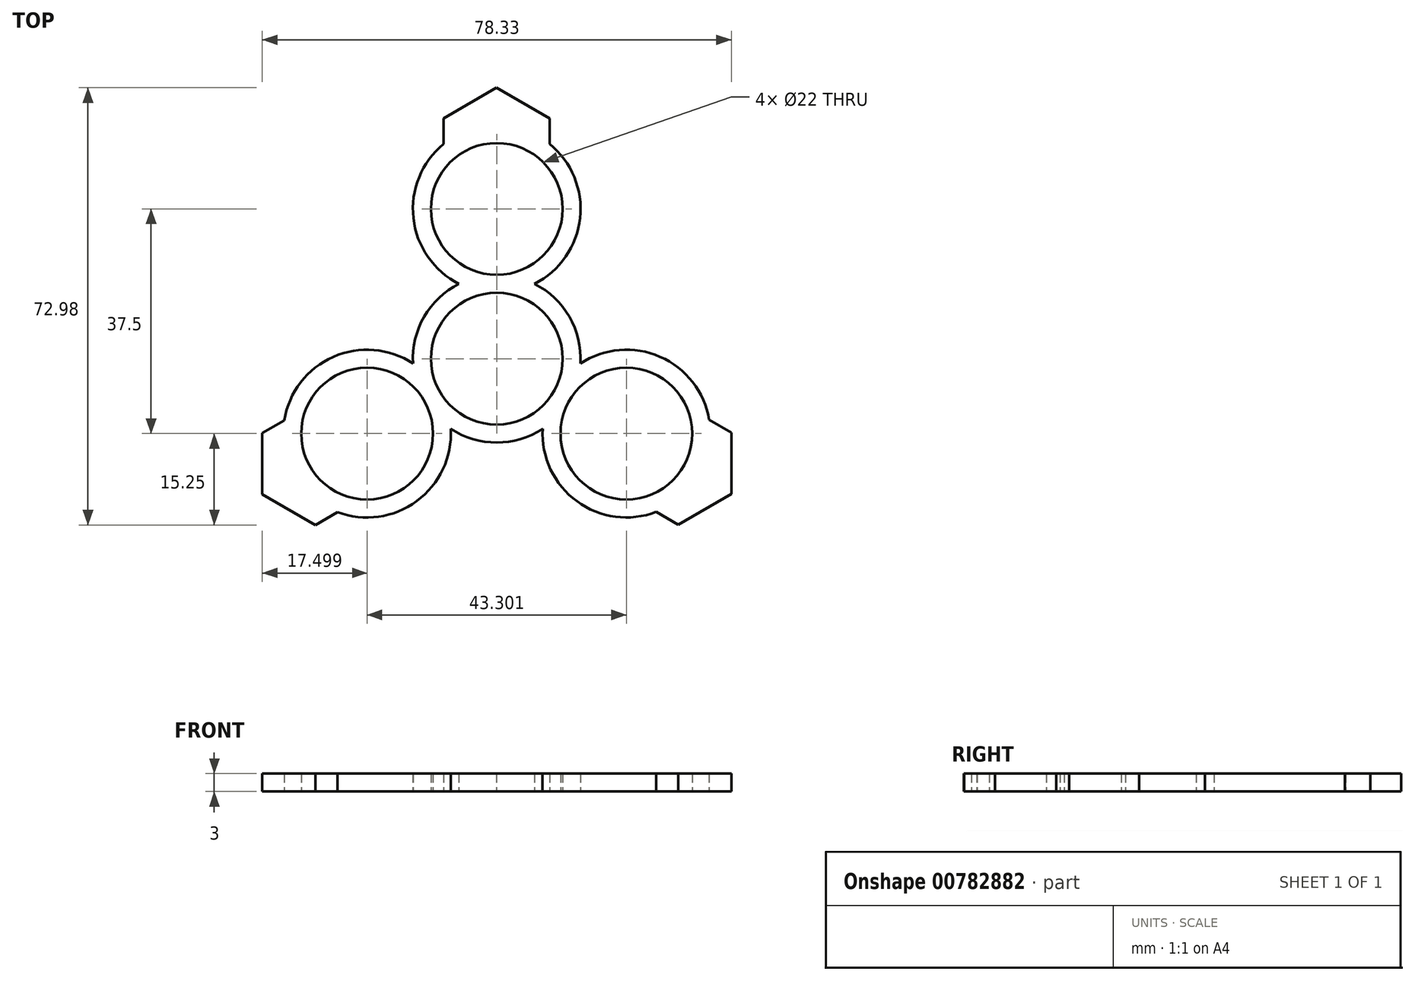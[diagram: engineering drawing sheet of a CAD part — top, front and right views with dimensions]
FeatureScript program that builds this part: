
annotation { "Feature Type Name" : "Feature", "Feature Type Description" : "" }
export const myFeature = defineFeature(function(context is Context, id is Id, definition is map)
    precondition{}
    {
        {
            var Q0;
            Q0=qCreatedBy(makeId("Top.planeOp"),FACE);
            var sketch = newSketch(context, id + "F0", { "sketchPlane" : qUnion([Q0])});
            skArc(sketch, "E0.1.0", {"start": v(-7.67, -11.71) * mm, "mid": v(-4, -13.42) * mm, "end": v(0, -14) * mm});
            skCircle(sketch, "E0.1.1", {"center": v(-21.65, -12.5) * mm, "radius": 11 * mm});
            skArc(sketch, "E0.1.2", {"start": v(-12.12, 7) * mm, "mid": v(-13.62, 3.24) * mm, "end": v(-13.98, -0.79) * mm});
            skArc(sketch, "E0.1.5", {"start": v(-9.53, 5.5) * mm, "mid": v(-9.53, -5.5) * mm, "end": v(0, -11) * mm});
            skArc(sketch, "E0.1.6", {"start": v(-13.98, -0.79) * mm, "mid": v(-27.3, 0.3) * mm, "end": v(-35.47, -10.29) * mm});
            skLineSegment(sketch, "E1.2", {"start": v(-30.3, -27.75) * mm, "end": v(-39.15, -22.64) * mm});
            skLineSegment(sketch, "E1.3", {"start": v(-39.15, -22.64) * mm, "end": v(-39.15, -12.41) * mm});
            skLineSegment(sketch, "E1.4", {"start": v(-39.15, -12.41) * mm, "end": v(-35.47, -10.29) * mm});
            skLineSegment(sketch, "E2.trimOffspring", {"start": v(-26.58, -25.6) * mm, "end": v(-30.3, -27.75) * mm});
            skLineSegment(sketch, "E3.trimOffspring", {"start": v(-21.45, -12.4) * mm, "end": v(-21.44, -12.41) * mm});
            skLineSegment(sketch, "E4.1.1", {"start": v(39.18, -22.59) * mm, "end": v(30.33, -27.7) * mm});
            skLineSegment(sketch, "E4.1.2", {"start": v(39.18, -12.36) * mm, "end": v(39.18, -22.59) * mm});
            skArc(sketch, "E4.1.3", {"start": v(7.67, -11.71) * mm, "mid": v(13.39, -23.8) * mm, "end": v(26.65, -25.58) * mm});
            skCircle(sketch, "E4.1.4", {"center": v(21.65, -12.5) * mm, "radius": 11 * mm});
            skArc(sketch, "E4.1.5", {"start": v(0, -11) * mm, "mid": v(9.53, -5.5) * mm, "end": v(9.53, 5.5) * mm});
            skArc(sketch, "E4.1.6", {"start": v(0, -14) * mm, "mid": v(4, -13.42) * mm, "end": v(7.67, -11.71) * mm});
            skArc(sketch, "E4.1.7", {"start": v(13.98, -0.79) * mm, "mid": v(13.62, 3.24) * mm, "end": v(12.12, 7) * mm});
            skLineSegment(sketch, "E4.1.8", {"start": v(35.46, -10.21) * mm, "end": v(39.18, -12.36) * mm});
            skLineSegment(sketch, "E4.1.9", {"start": v(30.33, -27.7) * mm, "end": v(26.65, -25.58) * mm});
            skLineSegment(sketch, "E4.1.10", {"start": v(21.47, -12.37) * mm, "end": v(21.47, -12.36) * mm});
            skLineSegment(sketch, "E4.2.1", {"start": v(-0.03, 45.23) * mm, "end": v(8.83, 40.11) * mm});
            skLineSegment(sketch, "E4.2.2", {"start": v(-8.89, 40.11) * mm, "end": v(-0.03, 45.23) * mm});
            skArc(sketch, "E4.2.3", {"start": v(6.3, 12.5) * mm, "mid": v(13.92, 23.5) * mm, "end": v(8.83, 35.87) * mm});
            skCircle(sketch, "E4.2.4", {"center": v(0, 25) * mm, "radius": 11 * mm});
            skArc(sketch, "E4.2.5", {"start": v(9.53, 5.5) * mm, "mid": v(0, 11) * mm, "end": v(-9.53, 5.5) * mm});
            skArc(sketch, "E4.2.6", {"start": v(12.12, 7) * mm, "mid": v(9.62, 10.17) * mm, "end": v(6.3, 12.5) * mm});
            skArc(sketch, "E4.2.7", {"start": v(-6.3, 12.5) * mm, "mid": v(-9.62, 10.17) * mm, "end": v(-12.12, 7) * mm});
            skLineSegment(sketch, "E4.2.8", {"start": v(-8.89, 35.82) * mm, "end": v(-8.89, 40.11) * mm});
            skLineSegment(sketch, "E4.2.9", {"start": v(8.83, 40.11) * mm, "end": v(8.83, 35.87) * mm});
            skLineSegment(sketch, "E4.2.10", {"start": v(-0.02, 24.78) * mm, "end": v(-0.03, 24.77) * mm});
            skArc(sketch, "E5.trimOffspring", {"start": v(-26.58, -25.6) * mm, "mid": v(-13.36, -23.78) * mm, "end": v(-7.67, -11.71) * mm});
            skArc(sketch, "E6.trimOffspring", {"start": v(35.46, -10.21) * mm, "mid": v(27.27, 0.32) * mm, "end": v(13.98, -0.79) * mm});
            skArc(sketch, "E7.trimOffspring", {"start": v(-8.89, 35.82) * mm, "mid": v(-13.92, 23.46) * mm, "end": v(-6.3, 12.5) * mm});
            skSolve(sketch);
        }
        {
            var Q0;
            Q0 = qSketchRegion(id + "F0", true);
            extrude(context, id + "F1", {"entities" : qUnion([Q0]), "depth" : 3 * mm, "offsetDistance" : 25 * mm});
        }
    });
